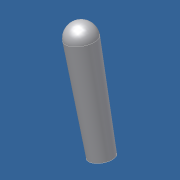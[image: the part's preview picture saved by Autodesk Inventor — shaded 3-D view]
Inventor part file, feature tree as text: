
AUTODESK INVENTOR PART (.ipt)
format: ipt  version: 2014 (Build 180170000, 170)  size: 96,768 bytes
history: native  units: in
note: dims shown in document units (in); Inventor stores cm internally (conversion verified against a paired STEP export)
features: other x14, revolve x1, sketch x1
ambient origin geometry x8: Origin, YZ Plane, XZ Plane, XY Plane, X Axis, Y Axis, Z Axis, Center Point
bodies: Solid1 (feature_tree)
feature tree (16):
  revolve  "Revolution1"  [1 undecoded]
  other  "rot_XY"
  other  "rot_YZ"
  other  "rot_ZX"
  other  "rot_X"
  other  "rot_Y"
  other  "rot_Z"
  other  "rot_Center"
  other  "to_cap_XY"
  other  "to_cap_YZ"
  other  "to_cap_ZX"
  other  "to_cap_X"
  other  "to_cap_Y"
  other  "to_cap_Z"
  other  "to_cap_Center"
  sketch  "Sketch_3"  dims[d0=360.0deg]
note: 1 required parameter value undecoded (feature->parameter linkage not recoverable at this tier; creation-order binding heuristic only, values carry confidence <= 0.55)
